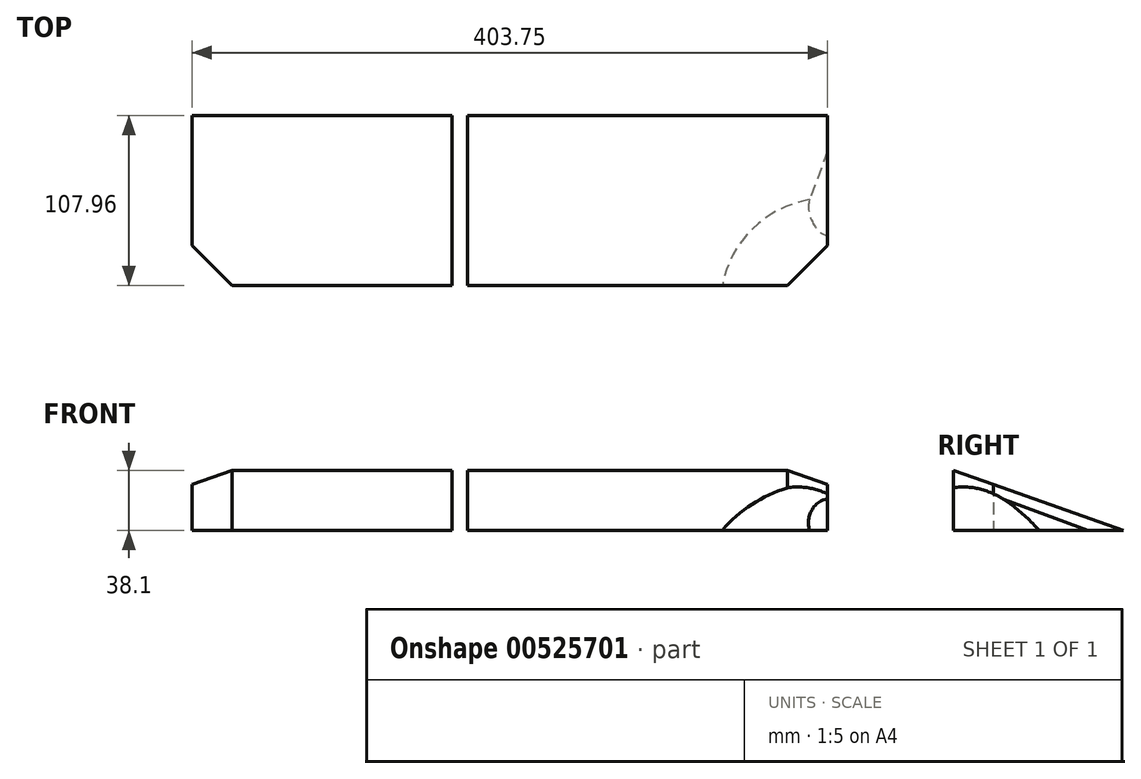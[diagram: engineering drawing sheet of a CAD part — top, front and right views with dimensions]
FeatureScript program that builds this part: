
annotation { "Feature Type Name" : "Feature", "Feature Type Description" : "" }
export const myFeature = defineFeature(function(context is Context, id is Id, definition is map)
    precondition{}
    {
        {
            var Q0;
            Q0=qCreatedBy(makeId("Top.planeOp"),FACE);
            var sketch = newSketch(context, id + "F0", { "sketchPlane" : qUnion([Q0])});
            skLineSegment(sketch, "E0.bottom", {"start": v(-82.55, 53.97) * mm, "end": v(82.55, 53.97) * mm});
            skLineSegment(sketch, "E0.top", {"start": v(-82.55, -53.98) * mm, "end": v(82.55, -53.98) * mm});
            skLineSegment(sketch, "E0.left", {"start": v(-82.55, 53.97) * mm, "end": v(-82.55, -53.98) * mm});
            skLineSegment(sketch, "E0.right", {"start": v(82.55, 53.97) * mm, "end": v(82.55, -53.98) * mm});
            skPoint(sketch, "E0.middle", {"position": v(0, 0) * mm});
            skLineSegment(sketch, "E1.bottom", {"start": v(-82.55, -53.98) * mm, "end": v(-57.15, -53.98) * mm});
            skLineSegment(sketch, "E1.top", {"start": v(-82.55, -28.57) * mm, "end": v(-57.15, -28.57) * mm});
            skLineSegment(sketch, "E1.left", {"start": v(-82.55, -53.98) * mm, "end": v(-82.55, -28.58) * mm});
            skLineSegment(sketch, "E1.right", {"start": v(-57.15, -53.98) * mm, "end": v(-57.15, -28.57) * mm});
            skLineSegment(sketch, "E2", {"start": v(-57.15, -53.98) * mm, "end": v(-82.55, -28.57) * mm});
            skSolve(sketch);
        }
        {
            var Q0;
            Q0=makeQuery(id+"F0.imprint","IMPRINT",FACE,{"disambiguationData":[TD([[makeQuery(id+"F0.imprint","IMPRINT",EDGE,{"derivedFrom":sQuery(id+"F0.wireOp",EDGE,"E0.bottom")}),-1.0]])]});
            var Q1;
            Q1=makeQuery(id+"F0.imprint","IMPRINT",FACE,{"disambiguationData":[TD([[makeQuery(id+"F0.imprint","IMPRINT",EDGE,{"derivedFrom":sQuery(id+"F0.wireOp",EDGE,"E1.top")}),-1.0]])]});
            extrude(context, id + "F1", {"entities" : qUnion([Q0, Q1]), "depth" : 38.1 * mm, "offsetDistance" : 25.4 * mm});
        }
        {
            var Q0;
            Q0=makeQuery(id+"F1.opExtrude","SWEPT_FACE",FACE,{"disambiguationData":[OSD([sQuery(id+"F0.wireOp",EDGE,"E0.right")])]});
            var sketch = newSketch(context, id + "F2", { "sketchPlane" : qUnion([Q0])});
            skLineSegment(sketch, "E3", {"start": v(53.97, 0) * mm, "end": v(-53.97, 38.1) * mm});
            skLineSegment(sketch, "E4", {"start": v(-53.97, 38.1) * mm, "end": v(53.98, 38.1) * mm});
            skLineSegment(sketch, "E5", {"start": v(53.98, 38.1) * mm, "end": v(53.97, 0) * mm});
            skSolve(sketch);
        }
        {
            var Q0;
            Q0=makeQuery(id+"F2.imprint","IMPRINT",FACE,{"disambiguationData":[TD([[makeQuery(id+"F2.imprint","IMPRINT",EDGE,{"derivedFrom":sQuery(id+"F2.wireOp",EDGE,"E3")}),-1.0]])]});
            extrude(context, id + "F3", {"entities" : qUnion([Q0]), "operationType" : NewBodyOperationType.REMOVE, "endBound" : BoundingType.UP_TO_NEXT, "oppositeDirection" : true, "depth" : 25.4 * mm, "offsetDistance" : 25.4 * mm});
        }
        {
            var Q0;
            Q0=qCreatedBy(makeId("Top.planeOp"),FACE);
            var sketch = newSketch(context, id + "F4", { "sketchPlane" : qUnion([Q0])});
            skLineSegment(sketch, "E6.bottom", {"start": v(92.6, 53.97) * mm, "end": v(321.2, 53.97) * mm});
            skLineSegment(sketch, "E6.top", {"start": v(92.6, -53.97) * mm, "end": v(321.2, -53.97) * mm});
            skLineSegment(sketch, "E6.left", {"start": v(92.6, 53.97) * mm, "end": v(92.6, -53.98) * mm});
            skLineSegment(sketch, "E6.right", {"start": v(321.2, 53.97) * mm, "end": v(321.2, -53.98) * mm});
            skSolve(sketch);
        }
        {
            var Q0;
            Q0=makeQuery(id+"F4.imprint","IMPRINT",FACE,{"disambiguationData":[TD([[makeQuery(id+"F4.imprint","IMPRINT",EDGE,{"derivedFrom":sQuery(id+"F4.wireOp",EDGE,"E6.bottom")}),-1.0]])]});
            extrude(context, id + "F5", {"entities" : qUnion([Q0]), "depth" : 38.1 * mm, "offsetDistance" : 25.4 * mm});
        }
        {
            var Q0;
            Q0=makeQuery(id+"F5.opExtrude","SWEPT_FACE",FACE,{"disambiguationData":[OSD([sQuery(id+"F4.wireOp",EDGE,"E6.right")])]});
            var sketch = newSketch(context, id + "F6", { "sketchPlane" : qUnion([Q0])});
            skLineSegment(sketch, "E7", {"start": v(53.97, 0) * mm, "end": v(-53.97, 38.1) * mm});
            skLineSegment(sketch, "E8", {"start": v(-53.98, 38.1) * mm, "end": v(53.97, 38.1) * mm});
            skLineSegment(sketch, "E9", {"start": v(53.97, 38.1) * mm, "end": v(53.97, 0) * mm});
            skSolve(sketch);
        }
        {
            var Q0;
            Q0=makeQuery(id+"F6.imprint","IMPRINT",FACE,{"disambiguationData":[TD([[makeQuery(id+"F6.imprint","IMPRINT",EDGE,{"derivedFrom":sQuery(id+"F6.wireOp",EDGE,"E7")}),-1.0]])]});
            extrude(context, id + "F7", {"entities" : qUnion([Q0]), "operationType" : NewBodyOperationType.REMOVE, "endBound" : BoundingType.UP_TO_NEXT, "oppositeDirection" : true, "depth" : 25.4 * mm, "offsetDistance" : 25.4 * mm});
        }
        {
            var Q0;
            Q0=makeQuery(id+"F5.opExtrude","SWEPT_FACE",FACE,{"disambiguationData":[OSD([sQuery(id+"F4.wireOp",EDGE,"E6.right")])]});
            var sketch = newSketch(context, id + "F8", { "sketchPlane" : qUnion([Q0])});
            skCircle(sketch, "E10", {"center": v(-66.68, -57.15) * mm, "radius": 88.9 * mm});
            skLineSegment(sketch, "E11", {"start": v(-66.68, 31.75) * mm, "end": v(-66.68, -146.05) * mm});
            skSolve(sketch);
        }
        {
            var Q0;
            {var subQ6=sQuery(id+"F8.wireOp",EDGE,"E11");Q0=makeQuery(id+"F8.imprint","IMPRINT",FACE,{"disambiguationData":[TD([[makeQuery(id+"F8.imprint","IMPRINT",EDGE,{"derivedFrom":subQ6}),1.0]])]});}
            var Q1;
            {var subQ0=sQuery(id+"F8.wireOp",EDGE,"E10");var subQ1=sQuery(id+"F4.wireOp",EDGE,"E6.right");var subQ4=makeQuery(id+"F5.opExtrude","CAP_EDGE",EDGE,{"disambiguationData":[OSD([subQ1])],"isStart":true});var subQ5=makeQuery(id+"F8.imprint","INTERSECT",VERTEX,{"derivedFrom":[subQ4,subQ0]});Q1=makeQuery(id+"F8.imprint","IMPRINT",FACE,{"disambiguationData":[TD([[makeQuery(id+"F8.imprint","IMPRINT",EDGE,{"disambiguationData":[TD([[subQ5,-1.0]])],"derivedFrom":subQ0}),1.0]])]});}
            var Q2;
            Q2=sQuery(id+"F8.wireOp",EDGE,"E11");
            revolve(context, id + "F9", {"operationType" : NewBodyOperationType.REMOVE, "entities" : qUnion([Q0, Q1]), "axis" : qUnion([Q2]), "revolveType" : RevolveType.FULL, "oppositeDirection" : true});
        }
        {
            var Q0;
            Q0=makeQuery(id+"F5.opExtrude","SWEPT_FACE",FACE,{"disambiguationData":[OSD([sQuery(id+"F4.wireOp",EDGE,"E6.right")])]});
            var sketch = newSketch(context, id + "F10", { "sketchPlane" : qUnion([Q0])});
            skLineSegment(sketch, "E12", {"start": v(-22.14, 19.8) * mm, "end": v(31.33, 0) * mm});
            skLineSegment(sketch, "E13", {"start": v(31.33, 0) * mm, "end": v(-22.14, 0) * mm});
            skLineSegment(sketch, "E14", {"start": v(-22.14, 0) * mm, "end": v(-22.14, 19.8) * mm});
            skSolve(sketch);
        }
        {
            var Q0;
            {var subQ0=sQuery(id+"F10.wireOp",EDGE,"E12");Q0=makeQuery(id+"F10.imprint","IMPRINT",FACE,{"disambiguationData":[TD([[makeQuery(id+"F10.imprint","IMPRINT",EDGE,{"derivedFrom":subQ0}),-1.0]])]});}
            var Q1;
            {var subQ3=sQuery(id+"F10.wireOp",EDGE,"E14");Q1=makeQuery(id+"F10.imprint","IMPRINT",FACE,{"disambiguationData":[TD([[makeQuery(id+"F10.imprint","IMPRINT",EDGE,{"derivedFrom":subQ3}),-1.0]])]});}
            var Q2;
            Q2=sQuery(id+"F10.wireOp",EDGE,"E13");
            revolve(context, id + "F11", {"operationType" : NewBodyOperationType.REMOVE, "entities" : qUnion([Q0, Q1]), "axis" : qUnion([Q2]), "revolveType" : RevolveType.FULL, "oppositeDirection" : true});
        }
        {
            var Q0;
            Q0=makeQuery(id+"F5.opExtrude","CAP_FACE",FACE,{"disambiguationData":[OSD([sQuery(id+"F4.wireOp",EDGE,"E6.bottom"),sQuery(id+"F4.wireOp",EDGE,"E6.top"),sQuery(id+"F4.wireOp",EDGE,"E6.left"),sQuery(id+"F4.wireOp",EDGE,"E6.right")])],"isStart":true});
            var sketch = newSketch(context, id + "F12", { "sketchPlane" : qUnion([Q0])});
            skLineSegment(sketch, "E15.bottom", {"start": v(321.2, 53.97) * mm, "end": v(295.8, 53.97) * mm});
            skLineSegment(sketch, "E15.top", {"start": v(321.2, 28.57) * mm, "end": v(295.8, 28.57) * mm});
            skLineSegment(sketch, "E15.left", {"start": v(321.2, 53.97) * mm, "end": v(321.2, 28.57) * mm});
            skLineSegment(sketch, "E15.right", {"start": v(295.8, 53.97) * mm, "end": v(295.8, 28.57) * mm});
            skLineSegment(sketch, "E16", {"start": v(321.2, 28.57) * mm, "end": v(295.8, 53.97) * mm});
            skSolve(sketch);
        }
        {
            var Q0;
            Q0=makeQuery(id+"F12.imprint","IMPRINT",FACE,{"disambiguationData":[TD([[makeQuery(id+"F12.imprint","IMPRINT",EDGE,{"derivedFrom":sQuery(id+"F12.wireOp",EDGE,"E15.bottom")}),1.0]])]});
            extrude(context, id + "F13", {"entities" : qUnion([Q0]), "operationType" : NewBodyOperationType.REMOVE, "oppositeDirection" : true, "depth" : 101.6 * mm, "offsetDistance" : 25.4 * mm});
        }
    });
